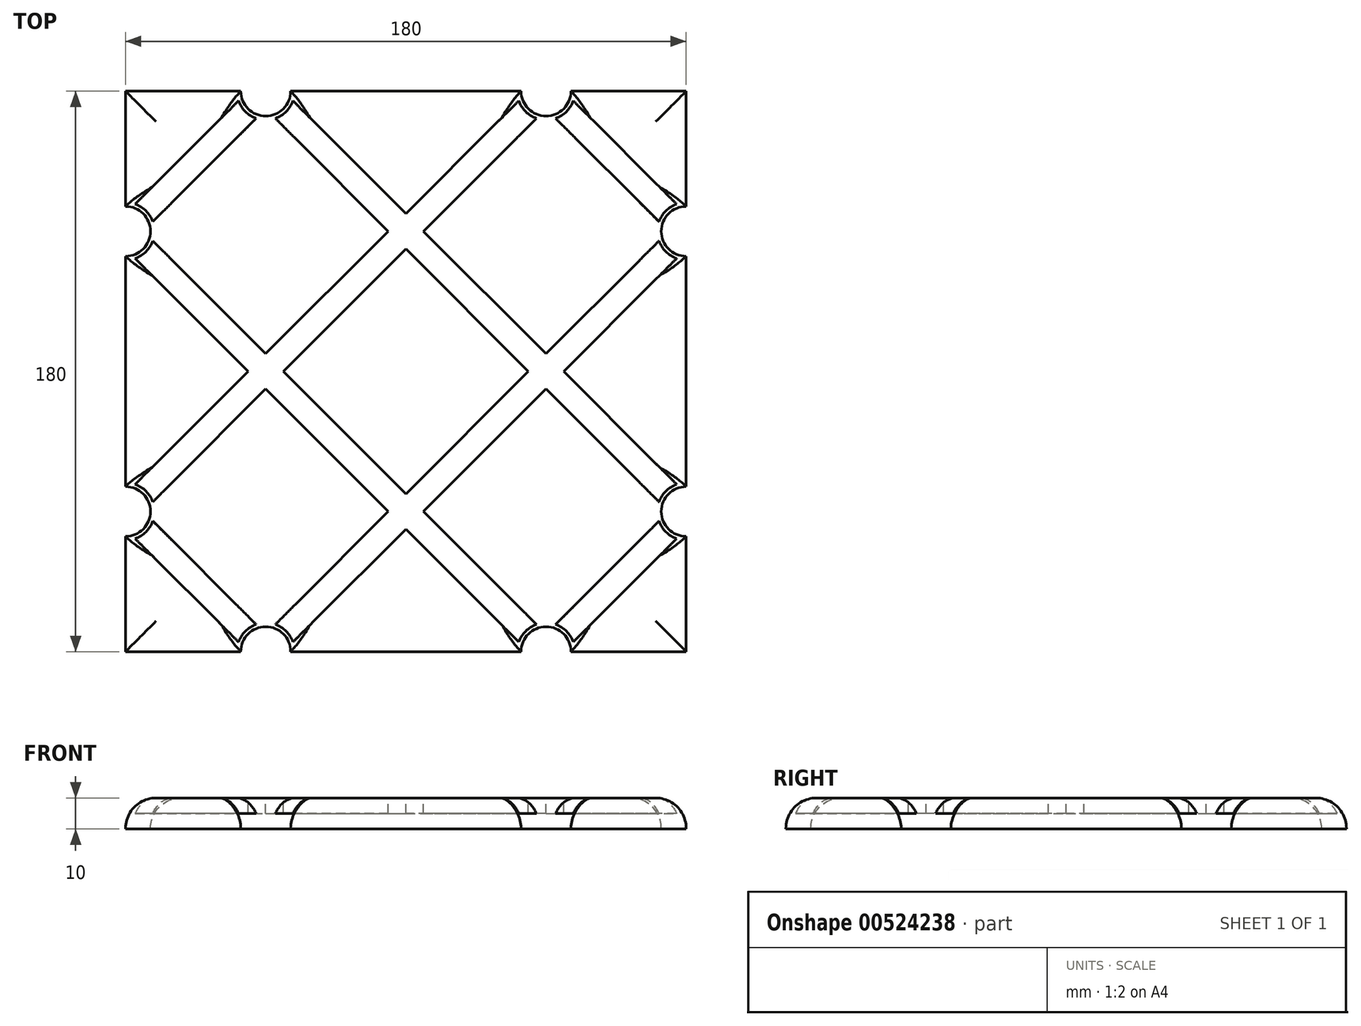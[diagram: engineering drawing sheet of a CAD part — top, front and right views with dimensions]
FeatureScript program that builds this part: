
annotation { "Feature Type Name" : "Feature", "Feature Type Description" : "" }
export const myFeature = defineFeature(function(context is Context, id is Id, definition is map)
    precondition{}
    {
        {
            var Q0;
            Q0=qCreatedBy(makeId("Top.planeOp"),FACE);
            var sketch = newSketch(context, id + "F0", { "sketchPlane" : qUnion([Q0])});
            skLineSegment(sketch, "E0.bottom", {"start": v(90, 90) * mm, "end": v(-90, 90) * mm});
            skLineSegment(sketch, "E0.top", {"start": v(90, -90) * mm, "end": v(-90, -90) * mm});
            skLineSegment(sketch, "E0.left", {"start": v(90, 90) * mm, "end": v(90, -90) * mm});
            skLineSegment(sketch, "E0.right", {"start": v(-90, 90) * mm, "end": v(-90, -90) * mm});
            skPoint(sketch, "E0.middle", {"position": v(0, 0) * mm});
            skLineSegment(sketch, "E1", {"start": v(-90, 45) * mm, "end": v(-45, 90) * mm});
            skLineSegment(sketch, "E2", {"start": v(-90, -45) * mm, "end": v(-45, 0) * mm});
            skLineSegment(sketch, "E3", {"start": v(-45, 0) * mm, "end": v(0, 45) * mm});
            skLineSegment(sketch, "E4", {"start": v(0, 45) * mm, "end": v(45, 90) * mm});
            skLineSegment(sketch, "E5", {"start": v(-45, -90) * mm, "end": v(0, -45) * mm});
            skLineSegment(sketch, "E6", {"start": v(0, -45) * mm, "end": v(45, 0) * mm});
            skLineSegment(sketch, "E7", {"start": v(45, 0) * mm, "end": v(90, 45) * mm});
            skLineSegment(sketch, "E8", {"start": v(45, -90) * mm, "end": v(90, -45) * mm});
            skLineSegment(sketch, "E9", {"start": v(45, -90) * mm, "end": v(0, -45) * mm});
            skLineSegment(sketch, "E10", {"start": v(0, -45) * mm, "end": v(-45, 0) * mm});
            skLineSegment(sketch, "E11", {"start": v(-45, 0) * mm, "end": v(-90, 45) * mm});
            skLineSegment(sketch, "E12", {"start": v(-45, 90) * mm, "end": v(0, 45) * mm});
            skLineSegment(sketch, "E13", {"start": v(0, 45) * mm, "end": v(45, 0) * mm});
            skLineSegment(sketch, "E14", {"start": v(45, 0) * mm, "end": v(90, -45) * mm});
            skLineSegment(sketch, "E15", {"start": v(-90, -45) * mm, "end": v(-45, -90) * mm});
            skLineSegment(sketch, "E16", {"start": v(45, 90) * mm, "end": v(90, 45) * mm});
            skSolve(sketch);
        }
        {
            var Q0;
            Q0=qCreatedBy(makeId("Top.planeOp"),FACE);
            var sketch = newSketch(context, id + "F1", { "sketchPlane" : qUnion([Q0])});
            skLineSegment(sketch, "E17.bottom", {"start": v(90, 90) * mm, "end": v(-90, 90) * mm});
            skLineSegment(sketch, "E17.top", {"start": v(90, -90) * mm, "end": v(-90, -90) * mm});
            skLineSegment(sketch, "E17.left", {"start": v(90, 90) * mm, "end": v(90, -90) * mm});
            skLineSegment(sketch, "E17.right", {"start": v(-90, 90) * mm, "end": v(-90, -90) * mm});
            skPoint(sketch, "E17.middle", {"position": v(0, 0) * mm});
            skSolve(sketch);
        }
        {
            var Q0;
            Q0=qCreatedBy(makeId("Top.planeOp"),FACE);
            var sketch = newSketch(context, id + "F2", { "sketchPlane" : qUnion([Q0])});
            skLineSegment(sketch, "E18", {"start": v(-90, 90) * mm, "end": v(-90, 53) * mm});
            skLineSegment(sketch, "E19", {"start": v(-90, 37) * mm, "end": v(-90, -37) * mm});
            skLineSegment(sketch, "E20", {"start": v(-90, -53) * mm, "end": v(-90, -90) * mm});
            skLineSegment(sketch, "E21", {"start": v(-90, -90) * mm, "end": v(-53, -90) * mm});
            skLineSegment(sketch, "E22", {"start": v(-37, -90) * mm, "end": v(37, -90) * mm});
            skLineSegment(sketch, "E23", {"start": v(53, -90) * mm, "end": v(90, -90) * mm});
            skLineSegment(sketch, "E24", {"start": v(90, -90) * mm, "end": v(90, -53) * mm});
            skLineSegment(sketch, "E25", {"start": v(90, -37) * mm, "end": v(90, 37) * mm});
            skLineSegment(sketch, "E26", {"start": v(90, 53) * mm, "end": v(90, 90) * mm});
            skLineSegment(sketch, "E27", {"start": v(90, 90) * mm, "end": v(53, 90) * mm});
            skLineSegment(sketch, "E28", {"start": v(37, 90) * mm, "end": v(-37, 90) * mm});
            skLineSegment(sketch, "E29", {"start": v(-90, 90) * mm, "end": v(-53, 90) * mm});
            skArc(sketch, "E30", {"start": v(-53, 90) * mm, "mid": v(-45, 82) * mm, "end": v(-37, 90) * mm});
            skArc(sketch, "E31", {"start": v(37, 90) * mm, "mid": v(45, 82) * mm, "end": v(53, 90) * mm});
            skArc(sketch, "E32", {"start": v(90, 53) * mm, "mid": v(82, 45) * mm, "end": v(90, 37) * mm});
            skArc(sketch, "E33", {"start": v(90, -37) * mm, "mid": v(82, -45) * mm, "end": v(90, -53) * mm});
            skArc(sketch, "E34", {"start": v(53, -90) * mm, "mid": v(45, -82) * mm, "end": v(37, -90) * mm});
            skArc(sketch, "E35", {"start": v(-37, -90) * mm, "mid": v(-45, -82) * mm, "end": v(-53, -90) * mm});
            skArc(sketch, "E36", {"start": v(-90, -53) * mm, "mid": v(-82, -45) * mm, "end": v(-90, -37) * mm});
            skArc(sketch, "E37", {"start": v(-90, 37) * mm, "mid": v(-82, 45) * mm, "end": v(-90, 53) * mm});
            skSolve(sketch);
        }
        {
            var Q0;
            Q0 = qSketchRegion(id + "F2", true);
            extrude(context, id + "F3", {"entities" : qUnion([Q0]), "depth" : 10 * mm, "offsetDistance" : 25 * mm});
        }
        {
            var Q0;
            Q0=makeQuery(id+"F3.opExtrude","CAP_FACE",FACE,{"disambiguationData":[OSD([sQuery(id+"F2.wireOp",EDGE,"E18"),sQuery(id+"F2.wireOp",EDGE,"E19"),sQuery(id+"F2.wireOp",EDGE,"E20"),sQuery(id+"F2.wireOp",EDGE,"E21"),sQuery(id+"F2.wireOp",EDGE,"E22"),sQuery(id+"F2.wireOp",EDGE,"E23"),sQuery(id+"F2.wireOp",EDGE,"E24"),sQuery(id+"F2.wireOp",EDGE,"E25"),sQuery(id+"F2.wireOp",EDGE,"E26"),sQuery(id+"F2.wireOp",EDGE,"E27"),sQuery(id+"F2.wireOp",EDGE,"E28"),sQuery(id+"F2.wireOp",EDGE,"E29"),sQuery(id+"F2.wireOp",EDGE,"E30"),sQuery(id+"F2.wireOp",EDGE,"E31"),sQuery(id+"F2.wireOp",EDGE,"E32"),sQuery(id+"F2.wireOp",EDGE,"E33"),sQuery(id+"F2.wireOp",EDGE,"E34"),sQuery(id+"F2.wireOp",EDGE,"E35"),sQuery(id+"F2.wireOp",EDGE,"E36"),sQuery(id+"F2.wireOp",EDGE,"E37")])],"isStart":false});
            var sketch = newSketch(context, id + "F4", { "sketchPlane" : qUnion([Q0])});
            skLineSegment(sketch, "E38", {"start": v(-90, 50.66) * mm, "end": v(-50.66, 90) * mm});
            skLineSegment(sketch, "E39", {"start": v(-50.66, 90) * mm, "end": v(-39.34, 90) * mm});
            skLineSegment(sketch, "E40", {"start": v(-39.34, 90) * mm, "end": v(0, 50.66) * mm});
            skLineSegment(sketch, "E41", {"start": v(0, 50.66) * mm, "end": v(39.34, 90) * mm});
            skLineSegment(sketch, "E42", {"start": v(39.34, 90) * mm, "end": v(50.66, 90) * mm});
            skLineSegment(sketch, "E43", {"start": v(50.66, 90) * mm, "end": v(90, 50.66) * mm});
            skLineSegment(sketch, "E44", {"start": v(90, 50.66) * mm, "end": v(90, 39.34) * mm});
            skLineSegment(sketch, "E45", {"start": v(90, 39.34) * mm, "end": v(50.66, 0) * mm});
            skLineSegment(sketch, "E46", {"start": v(50.66, 0) * mm, "end": v(90, -39.34) * mm});
            skLineSegment(sketch, "E47", {"start": v(90, -39.34) * mm, "end": v(90, -50.66) * mm});
            skLineSegment(sketch, "E48", {"start": v(90, -50.66) * mm, "end": v(50.66, -90) * mm});
            skLineSegment(sketch, "E49", {"start": v(50.66, -90) * mm, "end": v(39.34, -90) * mm});
            skLineSegment(sketch, "E50", {"start": v(39.34, -90) * mm, "end": v(0, -50.66) * mm});
            skLineSegment(sketch, "E51", {"start": v(0, -50.66) * mm, "end": v(-39.34, -90) * mm});
            skLineSegment(sketch, "E52", {"start": v(-39.34, -90) * mm, "end": v(-50.66, -90) * mm});
            skLineSegment(sketch, "E53", {"start": v(-50.66, -90) * mm, "end": v(-90, -50.66) * mm});
            skLineSegment(sketch, "E54", {"start": v(-90, -50.66) * mm, "end": v(-90, -39.34) * mm});
            skLineSegment(sketch, "E55", {"start": v(-90, -39.34) * mm, "end": v(-50.66, 0) * mm});
            skLineSegment(sketch, "E56", {"start": v(-50.66, 0) * mm, "end": v(-90, 39.34) * mm});
            skLineSegment(sketch, "E57", {"start": v(-90, 39.34) * mm, "end": v(-90, 50.66) * mm});
            skLineSegment(sketch, "E58", {"start": v(-84.34, 45) * mm, "end": v(-45, 5.66) * mm});
            skLineSegment(sketch, "E59", {"start": v(-45, 5.66) * mm, "end": v(-5.66, 45) * mm});
            skLineSegment(sketch, "E60", {"start": v(-5.66, 45) * mm, "end": v(-45, 84.34) * mm});
            skLineSegment(sketch, "E61", {"start": v(-45, 84.34) * mm, "end": v(-84.34, 45) * mm});
            skLineSegment(sketch, "E62", {"start": v(-45, -5.66) * mm, "end": v(-5.66, -45) * mm});
            skLineSegment(sketch, "E63", {"start": v(-5.66, -45) * mm, "end": v(-45, -84.34) * mm});
            skLineSegment(sketch, "E64", {"start": v(-45, -84.34) * mm, "end": v(-84.34, -45) * mm});
            skLineSegment(sketch, "E65", {"start": v(-84.34, -45) * mm, "end": v(-45, -5.66) * mm});
            skLineSegment(sketch, "E66", {"start": v(5.66, -45) * mm, "end": v(45, -5.66) * mm});
            skLineSegment(sketch, "E67", {"start": v(45, -5.66) * mm, "end": v(84.34, -45) * mm});
            skLineSegment(sketch, "E68", {"start": v(84.34, -45) * mm, "end": v(45, -84.34) * mm});
            skLineSegment(sketch, "E69", {"start": v(45, -84.34) * mm, "end": v(5.66, -45) * mm});
            skLineSegment(sketch, "E70", {"start": v(5.66, 45) * mm, "end": v(45, 84.34) * mm});
            skLineSegment(sketch, "E71", {"start": v(45, 84.34) * mm, "end": v(84.34, 45) * mm});
            skLineSegment(sketch, "E72", {"start": v(84.34, 45) * mm, "end": v(45, 5.66) * mm});
            skLineSegment(sketch, "E73", {"start": v(45, 5.66) * mm, "end": v(5.66, 45) * mm});
            skLineSegment(sketch, "E74", {"start": v(-39.34, 0) * mm, "end": v(0, 39.34) * mm});
            skLineSegment(sketch, "E75", {"start": v(0, 39.34) * mm, "end": v(39.34, 0) * mm});
            skLineSegment(sketch, "E76", {"start": v(39.34, 0) * mm, "end": v(0, -39.34) * mm});
            skLineSegment(sketch, "E77", {"start": v(0, -39.34) * mm, "end": v(-39.34, 0) * mm});
            skSolve(sketch);
        }
        {
            var Q0;
            Q0 = qSketchRegion(id + "F4", true);
            extrude(context, id + "F5", {"entities" : qUnion([Q0]), "operationType" : NewBodyOperationType.REMOVE, "oppositeDirection" : true, "depth" : 5 * mm, "offsetDistance" : 25 * mm});
        }
        {
            var Q0;
            Q0=makeQuery(id+"F3.opExtrude","CAP_EDGE",EDGE,{"disambiguationData":[OSD([sQuery(id+"F2.wireOp",EDGE,"E23")])],"isStart":false});
            var Q1;
            Q1=makeQuery(id+"F3.opExtrude","CAP_EDGE",EDGE,{"disambiguationData":[OSD([sQuery(id+"F2.wireOp",EDGE,"E24")])],"isStart":false});
            var Q2;
            Q2=makeQuery(id+"F3.opExtrude","CAP_EDGE",EDGE,{"disambiguationData":[OSD([sQuery(id+"F2.wireOp",EDGE,"E25")])],"isStart":false});
            var Q3;
            Q3=makeQuery(id+"F3.opExtrude","CAP_EDGE",EDGE,{"disambiguationData":[OSD([sQuery(id+"F2.wireOp",EDGE,"E26")])],"isStart":false});
            var Q4;
            Q4=makeQuery(id+"F3.opExtrude","CAP_EDGE",EDGE,{"disambiguationData":[OSD([sQuery(id+"F2.wireOp",EDGE,"E27")])],"isStart":false});
            var Q5;
            Q5=makeQuery(id+"F3.opExtrude","CAP_EDGE",EDGE,{"disambiguationData":[OSD([sQuery(id+"F2.wireOp",EDGE,"E28")])],"isStart":false});
            var Q6;
            Q6=makeQuery(id+"F3.opExtrude","CAP_EDGE",EDGE,{"disambiguationData":[OSD([sQuery(id+"F2.wireOp",EDGE,"E29")])],"isStart":false});
            var Q7;
            Q7=makeQuery(id+"F3.opExtrude","CAP_EDGE",EDGE,{"disambiguationData":[OSD([sQuery(id+"F2.wireOp",EDGE,"E18")])],"isStart":false});
            var Q8;
            Q8=makeQuery(id+"F3.opExtrude","CAP_EDGE",EDGE,{"disambiguationData":[OSD([sQuery(id+"F2.wireOp",EDGE,"E19")])],"isStart":false});
            var Q9;
            Q9=makeQuery(id+"F3.opExtrude","CAP_EDGE",EDGE,{"disambiguationData":[OSD([sQuery(id+"F2.wireOp",EDGE,"E22")])],"isStart":false});
            var Q10;
            Q10=makeQuery(id+"F3.opExtrude","CAP_EDGE",EDGE,{"disambiguationData":[OSD([sQuery(id+"F2.wireOp",EDGE,"E21")])],"isStart":false});
            var Q11;
            Q11=makeQuery(id+"F3.opExtrude","CAP_EDGE",EDGE,{"disambiguationData":[OSD([sQuery(id+"F2.wireOp",EDGE,"E20")])],"isStart":false});
            var Q12;
            {var subQ0=sQuery(id+"F2.wireOp",EDGE,"E30");Q12=makeQuery(id+"F5.boolean.opBoolean","SPLIT",EDGE,{"disambiguationData":[TD([makeQuery(id+"F5.opExtrude","SWEPT_FACE",FACE,{"disambiguationData":[OSD([sQuery(id+"F4.wireOp",EDGE,"E60")])]})])],"derivedFrom":makeQuery(id+"F3.opExtrude","CAP_EDGE",EDGE,{"disambiguationData":[OSD([subQ0])],"isStart":false})});}
            var Q13;
            {var subQ0=sQuery(id+"F2.wireOp",EDGE,"E37");Q13=makeQuery(id+"F5.boolean.opBoolean","SPLIT",EDGE,{"disambiguationData":[TD([makeQuery(id+"F5.opExtrude","SWEPT_FACE",FACE,{"disambiguationData":[OSD([sQuery(id+"F4.wireOp",EDGE,"E58")])]})])],"derivedFrom":makeQuery(id+"F3.opExtrude","CAP_EDGE",EDGE,{"disambiguationData":[OSD([subQ0])],"isStart":false})});}
            var Q14;
            {var subQ0=sQuery(id+"F2.wireOp",EDGE,"E36");Q14=makeQuery(id+"F5.boolean.opBoolean","SPLIT",EDGE,{"disambiguationData":[TD([makeQuery(id+"F5.opExtrude","SWEPT_FACE",FACE,{"disambiguationData":[OSD([sQuery(id+"F4.wireOp",EDGE,"E64")])]})])],"derivedFrom":makeQuery(id+"F3.opExtrude","CAP_EDGE",EDGE,{"disambiguationData":[OSD([subQ0])],"isStart":false})});}
            var Q15;
            {var subQ0=sQuery(id+"F2.wireOp",EDGE,"E35");Q15=makeQuery(id+"F5.boolean.opBoolean","SPLIT",EDGE,{"disambiguationData":[TD([makeQuery(id+"F5.opExtrude","SWEPT_FACE",FACE,{"disambiguationData":[OSD([sQuery(id+"F4.wireOp",EDGE,"E63")])]})])],"derivedFrom":makeQuery(id+"F3.opExtrude","CAP_EDGE",EDGE,{"disambiguationData":[OSD([subQ0])],"isStart":false})});}
            var Q16;
            {var subQ0=sQuery(id+"F2.wireOp",EDGE,"E34");Q16=makeQuery(id+"F5.boolean.opBoolean","SPLIT",EDGE,{"disambiguationData":[TD([makeQuery(id+"F5.opExtrude","SWEPT_FACE",FACE,{"disambiguationData":[OSD([sQuery(id+"F4.wireOp",EDGE,"E68")])]})])],"derivedFrom":makeQuery(id+"F3.opExtrude","CAP_EDGE",EDGE,{"disambiguationData":[OSD([subQ0])],"isStart":false})});}
            var Q17;
            {var subQ0=sQuery(id+"F2.wireOp",EDGE,"E33");Q17=makeQuery(id+"F5.boolean.opBoolean","SPLIT",EDGE,{"disambiguationData":[TD([makeQuery(id+"F5.opExtrude","SWEPT_FACE",FACE,{"disambiguationData":[OSD([sQuery(id+"F4.wireOp",EDGE,"E67")])]})])],"derivedFrom":makeQuery(id+"F3.opExtrude","CAP_EDGE",EDGE,{"disambiguationData":[OSD([subQ0])],"isStart":false})});}
            var Q18;
            {var subQ0=sQuery(id+"F2.wireOp",EDGE,"E32");Q18=makeQuery(id+"F5.boolean.opBoolean","SPLIT",EDGE,{"disambiguationData":[TD([makeQuery(id+"F5.opExtrude","SWEPT_FACE",FACE,{"disambiguationData":[OSD([sQuery(id+"F4.wireOp",EDGE,"E71")])]})])],"derivedFrom":makeQuery(id+"F3.opExtrude","CAP_EDGE",EDGE,{"disambiguationData":[OSD([subQ0])],"isStart":false})});}
            var Q19;
            {var subQ0=sQuery(id+"F2.wireOp",EDGE,"E31");Q19=makeQuery(id+"F5.boolean.opBoolean","SPLIT",EDGE,{"disambiguationData":[TD([makeQuery(id+"F5.opExtrude","SWEPT_FACE",FACE,{"disambiguationData":[OSD([sQuery(id+"F4.wireOp",EDGE,"E70")])]})])],"derivedFrom":makeQuery(id+"F3.opExtrude","CAP_EDGE",EDGE,{"disambiguationData":[OSD([subQ0])],"isStart":false})});}
            fillet(context, id + "F6", {"entities" : qUnion([Q0, Q1, Q2, Q3, Q4, Q5, Q6, Q7, Q8, Q9, Q10, Q11, Q12, Q13, Q14, Q15, Q16, Q17, Q18, Q19]), "radius" : 9.79 * mm, "tangentPropagation" : true, "allowEdgeOverflow" : false});
        }
    });
